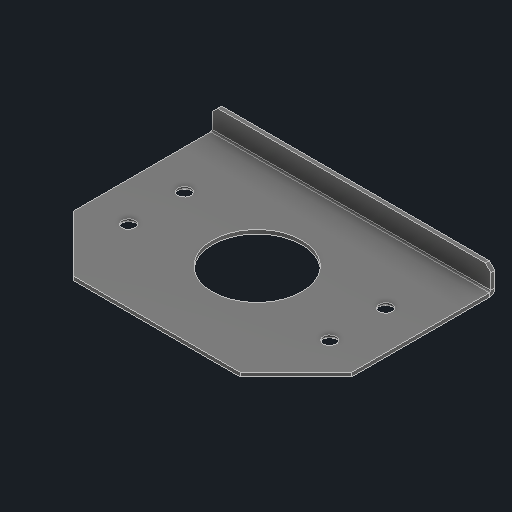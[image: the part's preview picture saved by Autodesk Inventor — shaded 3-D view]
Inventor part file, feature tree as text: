
AUTODESK INVENTOR PART (.ipt)
format: ipt  version: 2024 (Build 280153000, 153)  size: 116,224 bytes
history: native  units: in
note: dims shown in document units (in); Inventor stores cm internally (conversion verified against a paired STEP export)
features: mirror x1
ambient origin geometry x8: Origin, YZ Plane, XZ Plane, XY Plane, X Axis, Y Axis, Z Axis, Center Point
bodies: Solid1 (feature_tree)
feature tree (1):
  mirror  "Mirror1"
